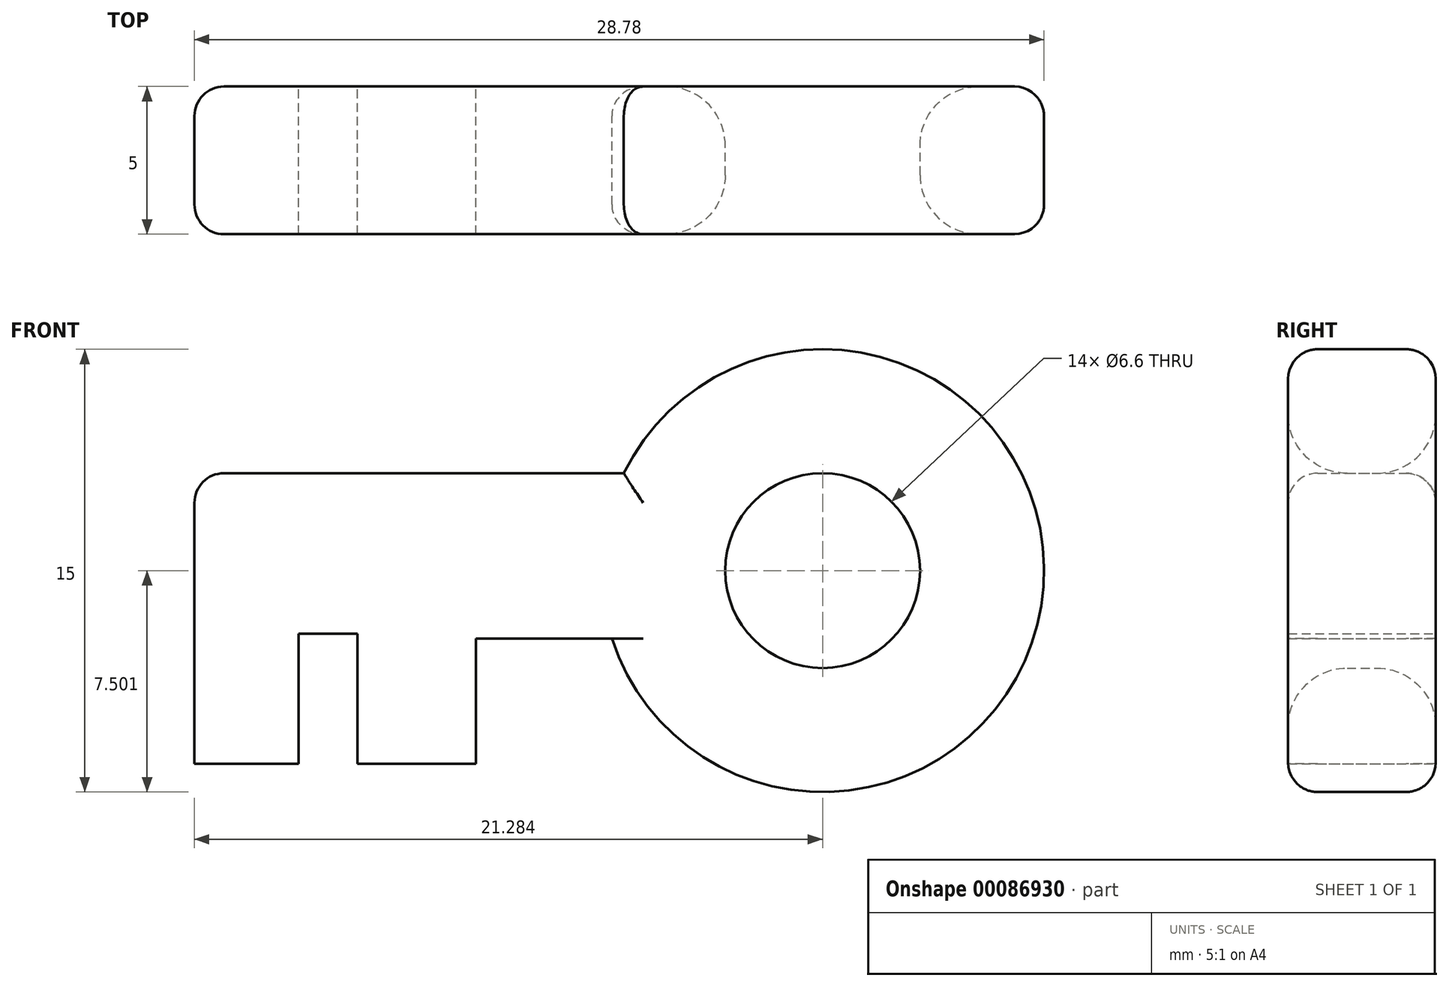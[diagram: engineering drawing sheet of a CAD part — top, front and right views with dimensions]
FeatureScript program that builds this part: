
annotation { "Feature Type Name" : "Feature", "Feature Type Description" : "" }
export const myFeature = defineFeature(function(context is Context, id is Id, definition is map)
    precondition{}
    {
        {
            var Q0;
            Q0=qCreatedBy(makeId("Front.planeOp"),FACE);
            var sketch = newSketch(context, id + "F0", { "sketchPlane" : qUnion([Q0])});
            skCircle(sketch, "E0", {"center": v(-3, 6.54) * mm, "radius": 7.5 * mm});
            skLineSegment(sketch, "E1", {"start": v(-9.73, 9.84) * mm, "end": v(-24.28, 9.84) * mm});
            skLineSegment(sketch, "E2", {"start": v(-24.28, 9.84) * mm, "end": v(-24.28, 0) * mm});
            skLineSegment(sketch, "E3", {"start": v(-24.28, 0) * mm, "end": v(-20.75, 0) * mm});
            skLineSegment(sketch, "E4", {"start": v(-20.75, 0) * mm, "end": v(-20.75, 4.4) * mm});
            skLineSegment(sketch, "E5", {"start": v(-20.75, 4.4) * mm, "end": v(-18.75, 4.4) * mm});
            skLineSegment(sketch, "E6", {"start": v(-18.75, 4.4) * mm, "end": v(-18.75, 0) * mm});
            skLineSegment(sketch, "E7", {"start": v(-18.75, 0) * mm, "end": v(-14.74, 0) * mm});
            skLineSegment(sketch, "E8", {"start": v(-14.74, 0) * mm, "end": v(-14.74, 4.25) * mm});
            skLineSegment(sketch, "E9", {"start": v(-14.74, 4.25) * mm, "end": v(-10.14, 4.25) * mm});
            skCircle(sketch, "E10", {"center": v(-3, 6.54) * mm, "radius": 3.3 * mm});
            skSolve(sketch);
        }
        {
            var Q0;
            {var subQ1=sQuery(id+"F0.wireOp",EDGE,"E1");Q0=makeQuery(id+"F0.imprint","IMPRINT",FACE,{"disambiguationData":[TD([[makeQuery(id+"F0.imprint","IMPRINT",EDGE,{"derivedFrom":subQ1}),1.0]])]});}
            var Q1;
            Q1=makeQuery(id+"F0.imprint","IMPRINT",FACE,{"disambiguationData":[TD([[makeQuery(id+"F0.imprint","IMPRINT",EDGE,{"derivedFrom":sQuery(id+"F0.wireOp",EDGE,"E10")}),-1.0]])]});
            extrude(context, id + "F1", {"entities" : qUnion([Q0, Q1]), "depth" : 5 * mm});
        }
        {
            var Q0;
            Q0=makeQuery(id+"F1.opExtrude","CAP_EDGE",EDGE,{"disambiguationData":[OSD([sQuery(id+"F0.wireOp",EDGE,"E1")])],"isStart":false});
            var Q1;
            Q1=makeQuery(id+"F1.opExtrude","CAP_EDGE",EDGE,{"disambiguationData":[OSD([sQuery(id+"F0.wireOp",EDGE,"E1")])],"isStart":true});
            var Q2;
            Q2=makeQuery(id+"F1.opExtrude","CAP_EDGE",EDGE,{"disambiguationData":[OSD([sQuery(id+"F0.wireOp",EDGE,"E2")])],"isStart":true});
            var Q3;
            Q3=makeQuery(id+"F1.opExtrude","SWEPT_EDGE",EDGE,{"disambiguationData":[OSD([sQuery(id+"F0.wireOp",EDGE,"E1"),sQuery(id+"F0.wireOp",EDGE,"E2")])]});
            var Q4;
            Q4=makeQuery(id+"F1.opExtrude","CAP_EDGE",EDGE,{"disambiguationData":[OSD([sQuery(id+"F0.wireOp",EDGE,"E2")])],"isStart":false});
            var Q5;
            Q5=makeQuery(id+"F1.opExtrude","CAP_EDGE",EDGE,{"disambiguationData":[OSD([sQuery(id+"F0.wireOp",EDGE,"E0")])],"isStart":false});
            var Q6;
            Q6=makeQuery(id+"F1.opExtrude","CAP_EDGE",EDGE,{"disambiguationData":[OSD([sQuery(id+"F0.wireOp",EDGE,"E0")])],"isStart":true});
            fillet(context, id + "F2", {"entities" : qUnion([Q0, Q1, Q2, Q3, Q4, Q5, Q6]), "radius" : 1 * mm, "tangentPropagation" : true, "allowEdgeOverflow" : false});
        }
        {
            var Q0;
            Q0=makeQuery(id+"F1.opExtrude","CAP_EDGE",EDGE,{"disambiguationData":[OSD([sQuery(id+"F0.wireOp",EDGE,"E10")])],"isStart":true});
            fillet(context, id + "F3", {"entities" : qUnion([Q0]), "radius" : 2 * mm, "tangentPropagation" : true, "allowEdgeOverflow" : false});
        }
        {
            var Q0;
            Q0=makeQuery(id+"F1.opExtrude","CAP_EDGE",EDGE,{"disambiguationData":[OSD([sQuery(id+"F0.wireOp",EDGE,"E10")])],"isStart":false});
            fillet(context, id + "F4", {"entities" : qUnion([Q0]), "radius" : 2 * mm, "tangentPropagation" : true, "allowEdgeOverflow" : false});
        }
    });
